# Revit family: 3NDML
name_source: partatom
category: Mechanical Equipment
units: mm (PartAtom-declared; Revit-internal decimal feet)

## family parameters
Always vertical = Yes
Cut with Voids When Loaded = No
OmniClass Number = 23.40.40.11.17
OmniClass Title = Refrigerated Cases
Part Type = Normal
Room Calculation Point = No
Round Connector Dimension = Use Radius
Shared = No
Work Plane-Based = Yes

## types (9) — shared parameters
20" Shelf = Yes
ANTI CON AMPS = 0 A
BOTTOM ELECTRICAL = Yes
BOTTOM REFRIGERATION PIPING = Yes
Certifications = NSF 7, UL471, CSA
DATE = 05/06/2016
DEFROST AMPS = 0 A
DESIGNERS NAME = SHIDDRAMESH
DISCHARGE AIR TEMP = 34 °F
DISCHARGE AIR VELOCITY = 350 (FPM)
DRAIN HEATERS AMPS = 0 A
DRAIN LINE CONNECTION = SANITARY CONNECTION
DRAIN LINE DIAMETER = 2"
DRAIN PIPE TYPE = PVC
DRAIN PIPING = Yes
DRIP PAN PLUMB TYPE = HARD
Default Elevation = 48"
Defrost Num Day = 6
Defrost Termination = 42 °F
Defrost Type = TIMED-OFF DEFROST
Defrosts Per Day = 6
Description = Narrow Multi-Deck Merchandiser with Synerg-E™
EQUIPMENT DESCRIPTION = Narrow Multi-Deck Merchandiser with Synerg-E™
EQUIPMENT MARK = 3NDML-NRG
Evap Temp = 28
GLASS = Glass
HIGH EFFICIENCY FANS AMPS = 0 A
Height = 62"
High Power (Cornice) Amps = 0 A
High Power (Cornice) Watts = 30 W
Item Description = Narrow Multi-Deck Merchandiser with Synerg-E™
LF STD END = Yes
LIGHT AMPS = 0 A
LIQUID LINE CONNECTION = LIQUID LINE CONNECTION
LIQUID LINE DIAMETER = 0"
LIQUID LINE RADIUS = 0"
LOAD 1 CLASSIFICATION = Lighting
LOAD 1 DESCRIPTION = LIGHTS - STANDARD POWER (SHELF or CORNICE)
LOAD 1 PLUG TYPE = HARDWIRED
LOAD 1 POLES = 1
LOAD 1 VOLTAGE = 120 V
LOAD 2 CLASSIFICATION = Motor
LOAD 2 DESCRIPTION = HIGH EFFICIENCY FANS CONNECTION
LOAD 2 PLUG TYPE = HARDWIRED
LOAD 2 POLES = 1
LOAD 2 VOLTAGE = 120 V
LOAD 3 CLASSIFICATION = Power
LOAD 3 DESCRIPTION = ANTI-SWEAT CONNECTION
LOAD 3 PLUG TYPE = HARDWIRED
LOAD 3 POLES = 1
LOAD 3 VOLTAGE = 120 V
LOAD 3 WATTAGE = 0 W
LOAD 4 DESCRIPTION = DEFROST HEATER CONNECTION
LOAD 4 PLUG TYPE = HARDWIRED
LOAD 4 POLES = 1
LOAD 4 VOLTAGE = 208 V
LOAD 4 WATTAGE = 0 W
LOAD 5 DESCRIPTION = DRAIN HEATER CONNECTION
LOAD 5 PLUG TYPE = HARDWIRED
LOAD 5 POLES = 1
LOAD 5 VOLTAGE = 120 V
LOAD 5 WATTAGE = 0 W
Legend Number = 3NDML-NRG
Light Length = 3'
Lights Per Row = 2
Load Mbh = 1.259
Manufacturer = HILL PHOENIX
Model = 3NDML-NRG
Number of Fans = 2
PAINTED METAL UPPER SHELF = PAINTED SHELVES
POWER FACTOR = 1
PRESSURE REGULATOR = 0.00 psi
REFRIGERATION PIPING = COPPER PIPE
RT STD END = Yes
Refrig Charge Lbs = -
Run-Off Time (Min) = 6-8 (Min)
SANITARY PIPE SIZE = 1"
STAINLESS STEEL = GALVANIZED STEEL
SUCTION LINE CONNECTION = SUCTION LINE CONNECTION
SUCTION LINE DIAMETER = 1"
SUCTION LINE RADIUS = 0"
Standard Power Amps = 0 A
Standard Power Watts = 17 W
Superheat Set Point @ Bulb (°F) = 6-8 °F
TOP ELECTRICAL = Yes
TOP REFRIGERATION PIPING = Yes
Timed-Off Defrost Termination Temp = 42 °F
URL = http://www.hillphoenix.com
Width = 35 7/8"

## per-type parameters (varying)
| type | Application Discipline | BTUH Conventional | BTUH Parallel | DRAIN LINE | Discharge Air (°F) | Discharge Air Velocity (FPM) | Evaporator (°F) | High Efficiency Amps | High Efficiency Watts | LOAD 1 WATTAGE | LOAD 2 WATTAGE | Length | Timed-Off Defrost Fail-Safe (Min) |
| 4' |  | 0 | 0 | 48" | -460 °F | 350 FPM | -460 °F | 1 A | 53 W | 0 W | 0 W | 96" | 42 (Min) |
| 6' |  | 0 | 0 | 36" | -460 °F | 350 FPM | -460 °F | 1 A | 53 W | 17 W | 53 W | 72" | 42 (Min) |
| 8' |  | 0 | 0 | 48" | -460 °F | 350 FPM | -460 °F | 0 A | 0 W | 0 W | 0 W | 96" | 42 (Min) |
| 12' |  | 0 | 0 | 72" | -460 °F | 350 FPM | -460 °F | 1 A | 53 W | 0 W | 0 W | 144" | 42 (Min) |
| 06' Produce/Beverage | Produce/Beverage | 1167 | 1225 | 36" | 37 °F | 210 FPM | 32 °F | 1 A | 53 W | 0 W | 0 W | 72" | 42 (Min) |
| 12' Dairy/Deli/Cut Produce |  | 0 | 0 | 72" | -460 °F | 350 FPM | -460 °F | 1 A | 53 W | 0 W | 0 W | 144" | 42 (Min) |
| 08' Dairy/Deli/Cut Produce |  | 0 | 0 | 48" | -460 °F | 350 FPM | -460 °F | 1 A | 53 W | 0 W | 0 W | 96" | 42 (Min) |
| 06' Dairy/Deli/Cut Produce | Dairy/Deli/Cut Produce | 1315 | 1343 | 36" | 33 °F | 210 FPM | 28 °F | 1 A | 65 W | 0 W | 0 W | 72" | 45 |
| 04' Dairy/Deli/Cut Produce |  | 0 | 0 | 24" | -460 °F | 350 FPM | -460 °F | 1 A | 53 W | 0 W | 0 W | 48" | 42 (Min) |

## geometry (parser evidence)
native form markers: Blend x12, Sweep x4
no freeform markers — native parametric forms only
